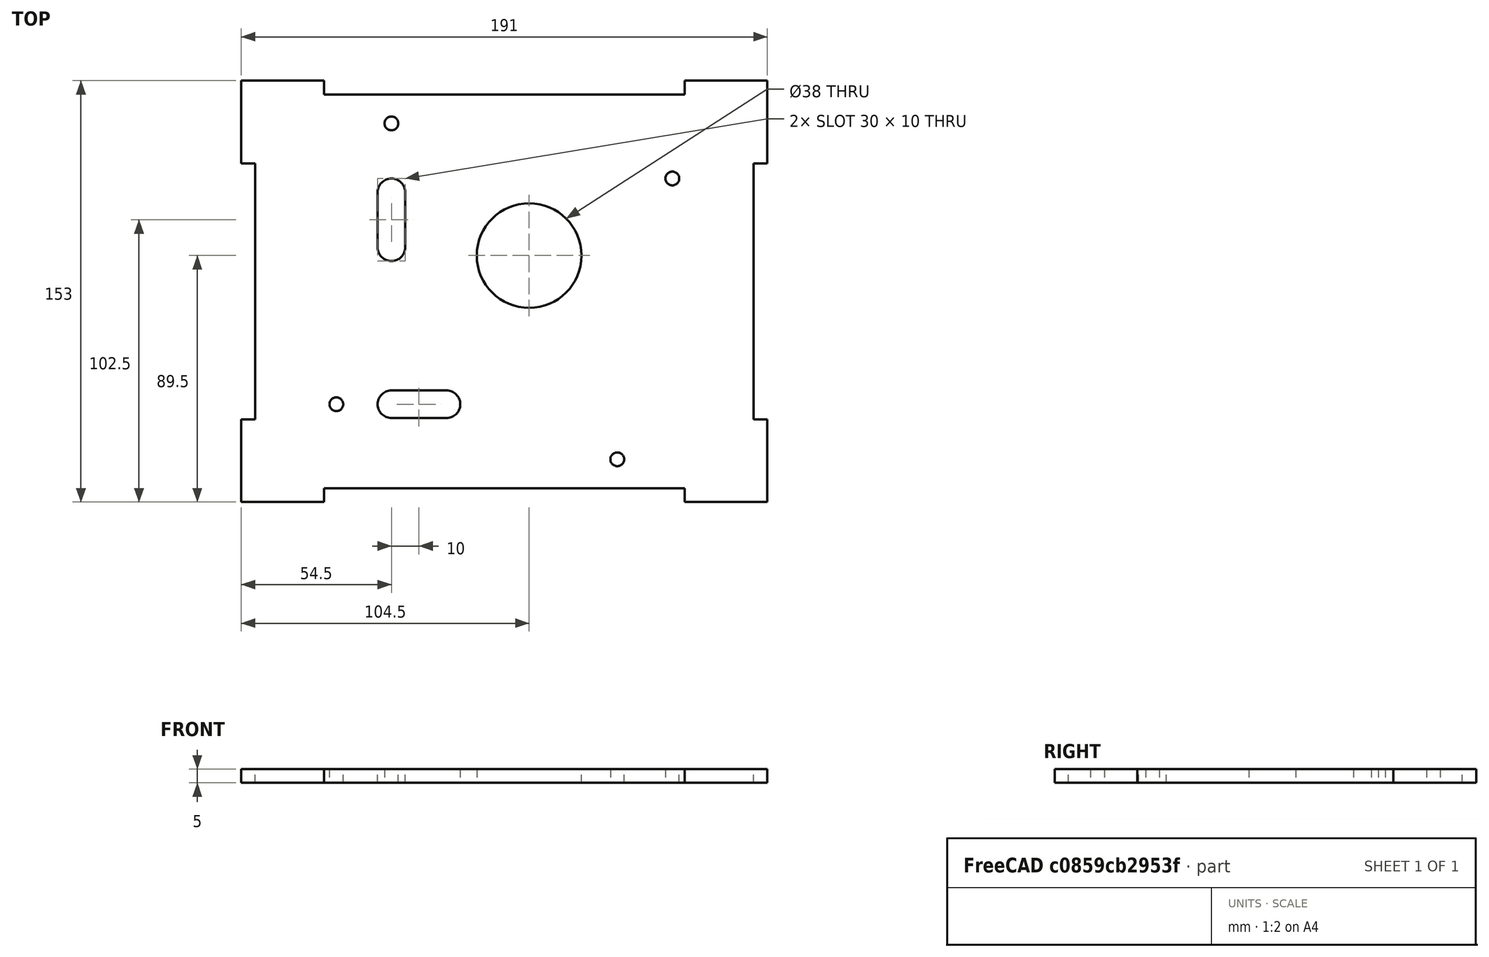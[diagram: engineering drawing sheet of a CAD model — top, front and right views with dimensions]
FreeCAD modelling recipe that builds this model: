
FCSTD DOCUMENT  (FreeCAD 0.15R4671 (Git))
Label: lower_bottom
License: All rights reserved
LicenseURL: http://en.wikipedia.org/wiki/All_rights_reserved
objects: Sketcher::SketchObject×1, PartDesign::Pad×1
note: 3 computed .brp shape members not serialized (recipe doc carries the construction recipe); baked Part::Feature solids carry a one-line shape summary decoded from their .brp

FEATURE [Sketcher::SketchObject] Sketch
  sketch-geometry (35):
    g0: LineSegment StartX=65.5 StartY=76.5 StartZ=0 EndX=95.5 EndY=76.5 EndZ=0
    g1: LineSegment StartX=95.5 StartY=76.5 StartZ=0 EndX=95.5 EndY=46.5 EndZ=0
    g2: LineSegment StartX=95.5 StartY=46.5 StartZ=0 EndX=90.5 EndY=46.5 EndZ=0
    g3: LineSegment StartX=90.5 StartY=46.5 StartZ=0 EndX=90.5 EndY=-46.5 EndZ=0
    g4: LineSegment StartX=90.5 StartY=-46.5 StartZ=0 EndX=95.5 EndY=-46.5 EndZ=0
    g5: LineSegment StartX=95.5 StartY=-46.5 StartZ=0 EndX=95.5 EndY=-76.5 EndZ=0
    g6: LineSegment StartX=95.5 StartY=-76.5 StartZ=0 EndX=65.5 EndY=-76.5 EndZ=0
    g7: LineSegment StartX=65.5 StartY=-76.5 StartZ=0 EndX=65.5 EndY=-71.5 EndZ=0
    g8: LineSegment StartX=65.5 StartY=-71.5 StartZ=0 EndX=-65.5 EndY=-71.5 EndZ=0
    g9: LineSegment StartX=-65.5 StartY=-71.5 StartZ=0 EndX=-65.5 EndY=-76.5 EndZ=0
    g10: LineSegment StartX=-65.5 StartY=-76.5 StartZ=0 EndX=-95.5 EndY=-76.5 EndZ=0
    g11: LineSegment StartX=-95.5 StartY=-76.5 StartZ=0 EndX=-95.5 EndY=-46.5 EndZ=0
    g12: LineSegment StartX=-95.5 StartY=-46.5 StartZ=0 EndX=-90.5 EndY=-46.5 EndZ=0
    g13: LineSegment StartX=-90.5 StartY=-46.5 StartZ=0 EndX=-90.5 EndY=46.5 EndZ=0
    g14: LineSegment StartX=-90.5 StartY=46.5 StartZ=0 EndX=-95.5 EndY=46.5 EndZ=0
    g15: LineSegment StartX=-95.5 StartY=46.5 StartZ=0 EndX=-95.5 EndY=76.5 EndZ=0
    g16: LineSegment StartX=-95.5 StartY=76.5 StartZ=0 EndX=-65.5 EndY=76.5 EndZ=0
    g17: LineSegment StartX=-65.5 StartY=76.5 StartZ=0 EndX=-65.5 EndY=71.5 EndZ=0
    g18: LineSegment StartX=-65.5 StartY=71.5 StartZ=0 EndX=65.5 EndY=71.5 EndZ=0
    g19: LineSegment StartX=65.5 StartY=71.5 StartZ=0 EndX=65.5 EndY=76.5 EndZ=0
    g20: Circle CenterX=-61 CenterY=-41 CenterZ=0 NormalX=0 NormalY=0 NormalZ=1 Radius=2.5
    g21: Circle CenterX=41 CenterY=-61 CenterZ=0 NormalX=0 NormalY=0 NormalZ=1 Radius=2.5
    g22: Circle CenterX=9 CenterY=13 CenterZ=0 NormalX=0 NormalY=0 NormalZ=1 Radius=19
    g23: Circle CenterX=61 CenterY=41 CenterZ=0 NormalX=0 NormalY=0 NormalZ=1 Radius=2.5
    g24: Circle CenterX=-41 CenterY=61 CenterZ=0 NormalX=0 NormalY=0 NormalZ=1 Radius=2.5
    g25: ArcOfCircle CenterX=-41 CenterY=36 CenterZ=0 NormalX=0 NormalY=0 NormalZ=1 Radius=5 StartAngle=0 EndAngle=3.14159
    g26: ArcOfCircle CenterX=-41 CenterY=16 CenterZ=0 NormalX=0 NormalY=0 NormalZ=1 Radius=5 StartAngle=3.14159 EndAngle=6.28319
    g27: LineSegment StartX=-46 StartY=36 StartZ=0 EndX=-46 EndY=16 EndZ=0
    g28: LineSegment StartX=-36 StartY=36 StartZ=0 EndX=-36 EndY=16 EndZ=0
    g29: ArcOfCircle CenterX=-41 CenterY=-41 CenterZ=0 NormalX=0 NormalY=0 NormalZ=1 Radius=5 StartAngle=1.5708 EndAngle=4.71239
    g30: ArcOfCircle CenterX=-21 CenterY=-41 CenterZ=0 NormalX=0 NormalY=0 NormalZ=1 Radius=5 StartAngle=4.71239 EndAngle=7.85398
    g31: LineSegment StartX=-41 StartY=-46 StartZ=0 EndX=-21 EndY=-46 EndZ=0
    g32: LineSegment StartX=-41 StartY=-36 StartZ=0 EndX=-21 EndY=-36 EndZ=0
    g33: LineSegment [constr] StartX=-41 StartY=61 StartZ=0 EndX=-41 EndY=36 EndZ=0
    g34: LineSegment [constr] StartX=-61 StartY=-41 StartZ=0 EndX=-41 EndY=-41 EndZ=0
  constraints (99):
    c: Coincident(g14,g15)
    c: Coincident(g13,g14)
    c: Coincident(g15,g16)
    c: Coincident(g16,g17)
    c: Coincident(g17,g18)
    c: Coincident(g18,g19)
    c: Coincident(g0,g19)
    c: Coincident(g0,g1)
    c: Coincident(g1,g2)
    c: Coincident(g2,g3)
    c: Coincident(g3,g4)
    c: Coincident(g4,g5)
    c: Coincident(g5,g6)
    c: Coincident(g6,g7)
    c: Coincident(g7,g8)
    c: Coincident(g8,g9)
    c: Coincident(g9,g10)
    c: Coincident(g10,g11)
    c: Coincident(g11,g12)
    c: Coincident(g12,g13)
    c: Vertical(g15)
    c: Vertical(g17)
    c: Vertical(g19)
    c: Vertical(g1)
    c: Vertical(g5)
    c: Vertical(g7)
    c: Vertical(g9)
    c: Vertical(g11)
    c: Vertical(g13)
    c: Horizontal(g16)
    c: Horizontal(g18)
    c: Horizontal(g0)
    c: Horizontal(g2)
    c: Horizontal(g14)
    c: Horizontal(g12)
    c: Horizontal(g4)
    c: Horizontal(g6)
    c: Horizontal(g8)
    c: Horizontal(g10)
    c: Equal(g10,g11)
    c: Equal(g11,g6)
    c: Equal(g6,g5)
    c: Equal(g5,g1)
    c: Equal(g1,g0)
    c: Equal(g0,g16)
    c: Equal(g16,g15)
    c: Equal(g14,g17)
    c: Equal(g17,g19)
    c: Equal(g19,g2)
    c: Equal(g2,g4)
    c: Equal(g9,g12)
    c: DistanceX(g12) = 5
    c: DistanceY(g17,g8) = -143
    c: DistanceX(g12,g3) = 181
    c: Vertical(g3)
    c: DistanceY(g15) = 30
    c: Radius(g22) = 19
    c: DistanceX(g22,g18) = 56.5
    c: DistanceY(g22,g18) = 58.5
    c: Tangent(g25,g28) = 1.5708
    c: Tangent(g25,g27) = -1.5708
    c: Tangent(g27,g26) = -1.5708
    c: Tangent(g28,g26) = 1.5708
    c: Vertical(g27)
    c: Equal(g25,g26)
    c: Radius(g25) = 5
    c: DistanceY(g25,g26) = -20
    c: Tangent(g29,g32) = 1.5708
    c: Tangent(g29,g31) = -1.5708
    c: Tangent(g31,g30) = -1.5708
    c: Tangent(g32,g30) = 1.5708
    c: Horizontal(g31)
    c: Equal(g29,g30)
    c: Radius(g29) = 5
    c: DistanceX(g29,g30) = 20
    c: Equal(g24,g20)
    c: Equal(g20,g21)
    c: Equal(g21,g23)
    c: Radius(g21) = 2.5
    c: DistanceX(g12,g20) = 29.5
    c: DistanceY(g20,g12) = -5.5
    c: DistanceX(g21,g7) = 24.5
    c: DistanceY(g7,g21) = 10.5
    c: DistanceY(g23,g2) = 5.5
    c: DistanceX(g23,g2) = 29.5
    c: DistanceY(g24,g17) = 10.5
    c: DistanceX(g24,g17) = -24.5
    c: Coincident(g33,g24)
    c: Coincident(g33,g25)
    c: Vertical(g33)
    c: DistanceY(g33) = -25
    c: Coincident(g34,g20)
    c: Coincident(g34,g29)
    c: Horizontal(g34)
    c: DistanceX(g34) = 20
    c: Symmetric(g0,g15,g-2)
    c: Symmetric(g0,g5,g-1)
    c: Equal(g4,g7)
    c: DistanceY(g7) = 5
FEATURE [PartDesign::Pad] Pad
  Length = 5
  Length2 = 100
  Midplane = true
  Sketch = -> Sketch
  Type = 0
